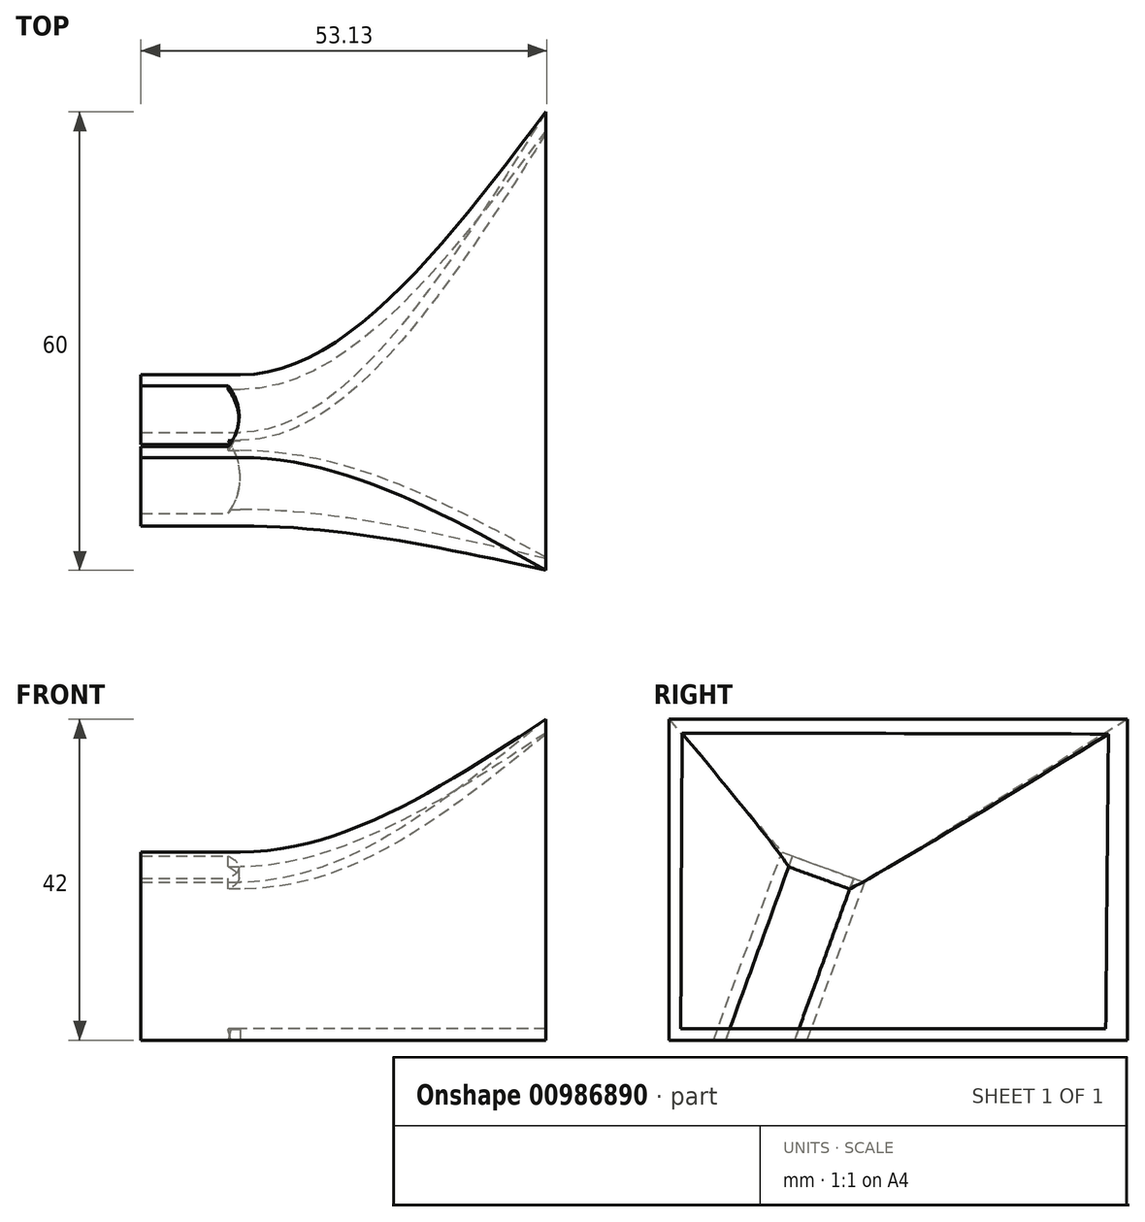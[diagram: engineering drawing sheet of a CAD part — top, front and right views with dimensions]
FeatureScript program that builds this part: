
annotation { "Feature Type Name" : "Feature", "Feature Type Description" : "" }
export const myFeature = defineFeature(function(context is Context, id is Id, definition is map)
    precondition{}
    {
        {
            var Q0;
            Q0=qCreatedBy(makeId("Top.planeOp"),FACE);
            var sketch = newSketch(context, id + "F0", { "sketchPlane" : qUnion([Q0])});
            skLineSegment(sketch, "E0", {"start": v(0, 6.05) * mm, "end": v(0, -6.05) * mm});
            skLineSegment(sketch, "E1", {"start": v(40, 30) * mm, "end": v(40, -30) * mm});
            skLineSegment(sketch, "E2", {"start": v(40, -30) * mm, "end": v(16.05, 0) * mm, "construction": true});
            skLineSegment(sketch, "E3", {"start": v(0, -6.05) * mm, "end": v(34.07, -6.05) * mm, "construction": true});
            skFitSpline(sketch, "E4", {"points": [v(0, -6.05) * mm, v(40, -30) * mm], "startDerivative": vector(33.29, 0) * mm, "endDerivative": vector(29.85, -37.4) * mm});
            skFitSpline(sketch, "E5.MirrorCS", {"points": [v(0, 6.05) * mm, v(40, 30) * mm], "startDerivative": vector(33.29, 0) * mm, "endDerivative": vector(29.85, 37.4) * mm});
            skSolve(sketch);
        }
        {
            var Q0;
            Q0=qCreatedBy(makeId("Right.planeOp"),FACE);
            var Q1;
            Q1=sQuery(id+"F0.wireOp",VERTEX,"E1.end");
            cPlane(context, id + "F1", {"entities" : qUnion([Q0, Q1]), "cplaneType" : CPlaneType.PLANE_POINT, "offset" : 25 * mm, "width" : 150 * mm, "height" : 150 * mm});
        }
        {
            var Q0;
            Q0=qCreatedBy(id+"F1.planeOp",FACE);
            var sketch = newSketch(context, id + "F2", { "sketchPlane" : qUnion([Q0])});
            skLineSegment(sketch, "E6.0", {"start": v(48, 0) * mm, "end": v(-12, 0) * mm});
            skLineSegment(sketch, "E7", {"start": v(-12, 0) * mm, "end": v(-12, 42) * mm});
            skLineSegment(sketch, "E8", {"start": v(-12, 42) * mm, "end": v(48, 42) * mm});
            skLineSegment(sketch, "E9", {"start": v(48, 42) * mm, "end": v(48, 0) * mm});
            skSolve(sketch);
        }
        {
            var Q0;
            Q0=qCreatedBy(makeId("Right.planeOp"),FACE);
            var sketch = newSketch(context, id + "F3", { "sketchPlane" : qUnion([Q0])});
            skPoint(sketch, "E10.0", {"position": v(6.05, 0) * mm});
            skLineSegment(sketch, "E11", {"start": v(-6.19, 0) * mm, "end": v(2.77, 24.6) * mm});
            skLineSegment(sketch, "E12", {"start": v(2.77, 24.6) * mm, "end": v(13.57, 20.67) * mm});
            skLineSegment(sketch, "E13", {"start": v(13.57, 20.67) * mm, "end": v(6.05, 0) * mm});
            skLineSegment(sketch, "E14", {"start": v(16.92, 0) * mm, "end": v(-15.5, 0) * mm, "construction": true});
            skLineSegment(sketch, "E15", {"start": v(6.05, 0) * mm, "end": v(-6.19, 0) * mm});
            skSolve(sketch);
        }
        {
            var Q0;
            Q0=sQuery(id+"F0.wireOp",EDGE,"E5.MirrorCS");
            var Q1;
            Q1=makeQuery(id+"F2.imprint","IMPRINT",FACE,{"disambiguationData":[TD([[makeQuery(id+"F2.imprint","IMPRINT",EDGE,{"derivedFrom":sQuery(id+"F2.wireOp",EDGE,"E6.0")}),-1.0]])]});
            var Q2;
            Q2=makeQuery(id+"F3.imprint","IMPRINT",FACE,{"disambiguationData":[TD([[makeQuery(id+"F3.imprint","IMPRINT",EDGE,{"derivedFrom":sQuery(id+"F3.wireOp",EDGE,"E11")}),-1.0]])]});
            var Q3;
            Q3=sQuery(id+"F0.wireOp",EDGE,"E5.MirrorCS");
            loft(context, id + "F4", {"spine" : qUnion([Q0]), "endCondition" : LoftEndDerivativeType.NORMAL_TO_PROFILE, "endMagnitude" : 1, "sheetProfilesArray" : [{ "sheetProfileEntities" : qUnion([Q1]) }, { "sheetProfileEntities" : qUnion([Q2]) }], "guidesArray" : [{ "guideEntities" : qUnion([Q3]), "guideDerivativeType" : LoftGuideDerivativeType.DEFAULT, "guideDerivativeMagnitude" : 1 }]});
        }
        {
            var Q0;
            Q0=makeQuery(id+"F4.opLoft","CAP_FACE",FACE,{"disambiguationData":[OSD([makeQuery(id+"F2.imprint","IMPRINT",FACE,{"disambiguationData":[TD([[makeQuery(id+"F2.imprint","IMPRINT",EDGE,{"derivedFrom":sQuery(id+"F2.wireOp",EDGE,"E6.0")}),-1.0]])]})])],"isStart":true});
            var Q1;
            Q1=makeQuery(id+"F4.opLoft","CAP_FACE",FACE,{"disambiguationData":[OSD([makeQuery(id+"F3.imprint","IMPRINT",FACE,{"disambiguationData":[TD([[makeQuery(id+"F3.imprint","IMPRINT",EDGE,{"derivedFrom":sQuery(id+"F3.wireOp",EDGE,"E11")}),-1.0]])]})])],"isStart":true});
            shell(context, id + "F5", {"entities" : qUnion([Q0, Q1]), "thickness" : 1.5 * mm});
        }
        {
            var Q0;
            Q0=qCreatedBy(makeId("Right.planeOp"),FACE);
            var sketch = newSketch(context, id + "F6", { "sketchPlane" : qUnion([Q0])});
            skLineSegment(sketch, "E16.0", {"start": v(13.57, 20.67) * mm, "end": v(6.05, 0) * mm});
            skLineSegment(sketch, "E16.3", {"start": v(2.77, 24.6) * mm, "end": v(4.18, 24.1) * mm});
            skLineSegment(sketch, "E16.4", {"start": v(-6.19, 0) * mm, "end": v(2.77, 24.6) * mm});
            skLineSegment(sketch, "E16.7", {"start": v(6.05, 0) * mm, "end": v(4.45, 0) * mm});
            skLineSegment(sketch, "E17.0", {"start": v(12.16, 21.19) * mm, "end": v(4.45, 0) * mm});
            skLineSegment(sketch, "E18.0", {"start": v(-4.6, 0) * mm, "end": v(4.18, 24.1) * mm});
            skLineSegment(sketch, "E19.trimOffspring", {"start": v(-4.6, 0) * mm, "end": v(-6.19, 0) * mm});
            skLineSegment(sketch, "E20.trimOffspring", {"start": v(12.16, 21.19) * mm, "end": v(13.57, 20.67) * mm});
            skSolve(sketch);
        }
        {
            var Q0;
            Q0=qSketchRegion(id+"F6",true);
            extrude(context, id + "F7", {"entities" : qUnion([Q0]), "operationType" : NewBodyOperationType.ADD, "oppositeDirection" : true, "depth" : 13 * mm, "offsetDistance" : 25 * mm});
        }
        {
            var Q0;
            Q0=qCreatedBy(makeId("Top.planeOp"),FACE);
            var sketch = newSketch(context, id + "F8", { "sketchPlane" : qUnion([Q0])});
            skLineSegment(sketch, "E21.0", {"start": v(0, 6.05) * mm, "end": v(0, -6.05) * mm, "construction": true});
            skLineSegment(sketch, "E21.1", {"start": v(-13, 4.45) * mm, "end": v(0, 4.45) * mm, "construction": true});
            skLineSegment(sketch, "E21.2", {"start": v(-13, -4.6) * mm, "end": v(0, -4.6) * mm, "construction": true});
            skLineSegment(sketch, "E22", {"start": v(-1.5, 4.45) * mm, "end": v(0, 4.45) * mm});
            skLineSegment(sketch, "E23", {"start": v(0, 4.45) * mm, "end": v(0, -4.6) * mm});
            skLineSegment(sketch, "E24", {"start": v(-1.5, -4.6) * mm, "end": v(0, -4.6) * mm});
            skLineSegment(sketch, "E25.0", {"start": v(-13, 4.95) * mm, "end": v(0.01, 4.95) * mm, "construction": true});
            skArc(sketch, "E26", {"start": v(-1.6, -4.6) * mm, "mid": v(-0.01, 0.18) * mm, "end": v(-1.59, 4.95) * mm});
            skLineSegment(sketch, "E27", {"start": v(-1.59, 4.95) * mm, "end": v(0.01, 4.95) * mm});
            skLineSegment(sketch, "E28", {"start": v(0.01, 4.95) * mm, "end": v(0, -4.6) * mm});
            skLineSegment(sketch, "E29", {"start": v(0, -4.6) * mm, "end": v(-1.6, -4.6) * mm});
            skSolve(sketch);
        }
        {
            var Q0;
            {var subQ4=sQuery(id+"F8.wireOp",EDGE,"E23");Q0=makeQuery(id+"F8.imprint","IMPRINT",FACE,{"disambiguationData":[TD([[makeQuery(id+"F8.imprint","IMPRINT",EDGE,{"derivedFrom":subQ4}),1.0]])]});}
            var Q1;
            {var subQ0=sQuery(id+"F8.wireOp",EDGE,"E23");Q1=makeQuery(id+"F8.imprint","IMPRINT",FACE,{"disambiguationData":[TD([[makeQuery(id+"F8.imprint","IMPRINT",EDGE,{"derivedFrom":subQ0}),-1.0]])]});}
            extrude(context, id + "F9", {"entities" : qUnion([Q0, Q1]), "operationType" : NewBodyOperationType.ADD, "depth" : 1.5 * mm, "offsetDistance" : 25 * mm});
        }
        {
            var Q0;
            Q0=makeQuery(id+"F7.opExtrude","SWEPT_FACE",FACE,{"disambiguationData":[OSD([sQuery(id+"F6.wireOp",EDGE,"E16.3")])]});
            var sketch = newSketch(context, id + "F10", { "sketchPlane" : qUnion([Q0])});
            skLineSegment(sketch, "E30.0", {"start": v(-13, -4.31) * mm, "end": v(0, -4.31) * mm, "construction": true});
            skLineSegment(sketch, "E30.1", {"start": v(-13, 4.19) * mm, "end": v(0, 4.19) * mm, "construction": true});
            skLineSegment(sketch, "E30.2", {"start": v(0.01, 4.65) * mm, "end": v(0, -4.31) * mm, "construction": true});
            skArc(sketch, "E31", {"start": v(-1.6, -4.31) * mm, "mid": v(-0.16, -0.06) * mm, "end": v(-1.6, 4.19) * mm});
            skLineSegment(sketch, "E32", {"start": v(-1.6, -4.31) * mm, "end": v(0, -4.31) * mm});
            skLineSegment(sketch, "E33", {"start": v(0, -4.31) * mm, "end": v(0, 4.19) * mm});
            skLineSegment(sketch, "E34", {"start": v(0, 4.19) * mm, "end": v(-1.6, 4.19) * mm});
            skSolve(sketch);
        }
        {
            var Q0;
            Q0=makeQuery(id+"F10.imprint","IMPRINT",FACE,{"disambiguationData":[TD([[makeQuery(id+"F10.imprint","IMPRINT",EDGE,{"derivedFrom":sQuery(id+"F10.wireOp",EDGE,"E31")}),-1.0]])]});
            extrude(context, id + "F11", {"entities" : qUnion([Q0]), "operationType" : NewBodyOperationType.ADD, "oppositeDirection" : true, "depth" : 1.5 * mm, "offsetDistance" : 25 * mm});
        }
    });
